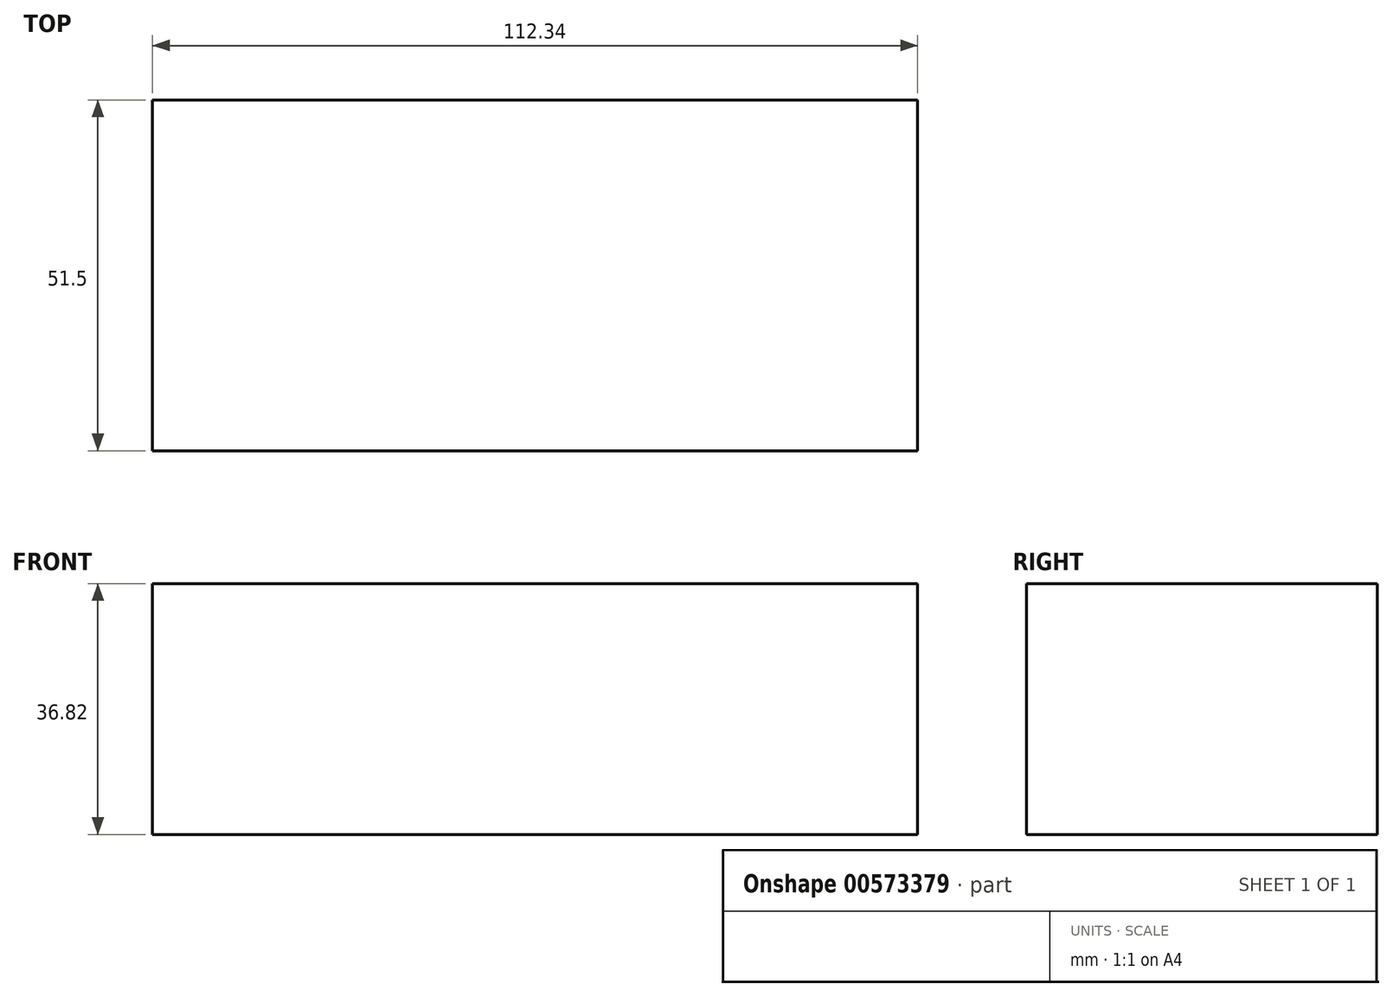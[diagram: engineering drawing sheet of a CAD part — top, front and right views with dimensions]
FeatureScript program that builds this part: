
annotation { "Feature Type Name" : "Feature", "Feature Type Description" : "" }
export const myFeature = defineFeature(function(context is Context, id is Id, definition is map)
    precondition{}
    {
        {
            var Q0;
            Q0=qCreatedBy(makeId("Top.planeOp"),FACE);
            var sketch = newSketch(context, id + "F0", { "sketchPlane" : qUnion([Q0])});
            skLineSegment(sketch, "E0.bottom", {"start": v(56.17, 25.75) * mm, "end": v(-56.17, 25.75) * mm});
            skLineSegment(sketch, "E0.top", {"start": v(56.17, -25.75) * mm, "end": v(-56.17, -25.75) * mm});
            skLineSegment(sketch, "E0.left", {"start": v(56.17, 25.75) * mm, "end": v(56.17, -25.75) * mm});
            skLineSegment(sketch, "E0.right", {"start": v(-56.17, 25.75) * mm, "end": v(-56.17, -25.75) * mm});
            skPoint(sketch, "E0.middle", {"position": v(0, 0) * mm});
            skSolve(sketch);
        }
        {
            var Q0;
            Q0=makeQuery(id+"F0.imprint","IMPRINT",FACE,{"disambiguationData":[TD([[makeQuery(id+"F0.imprint","IMPRINT",EDGE,{"derivedFrom":sQuery(id+"F0.wireOp",EDGE,"E0.bottom")}),1.0]])]});
            extrude(context, id + "F1", {"entities" : qUnion([Q0]), "endBound" : BoundingType.SYMMETRIC, "depth" : 36.83 * mm, "offsetDistance" : 25.4 * mm});
        }
        {
            var Q0;
            Q0=qCreatedBy(makeId("Top.planeOp"),FACE);
            var sketch = newSketch(context, id + "F2", { "sketchPlane" : qUnion([Q0])});
            skCircle(sketch, "E1", {"center": v(-35.07, 0) * mm, "radius": 11.74 * mm});
            skSolve(sketch);
        }
        {
            var Q0;
            Q0=sQuery(id+"F2.wireOp",EDGE,"E1");
            var Q1;
            Q1=makeQuery(id+"F1.opExtrude","CAP_EDGE",EDGE,{"disambiguationData":[OSD([sQuery(id+"F0.wireOp",EDGE,"E0.right")])],"isStart":true});
            revolve(context, id + "F3", {"bodyType" : ToolBodyType.SURFACE, "surfaceEntities" : qUnion([Q0]), "axis" : qUnion([Q1]), "revolveType" : RevolveType.FULL});
        }
    });
